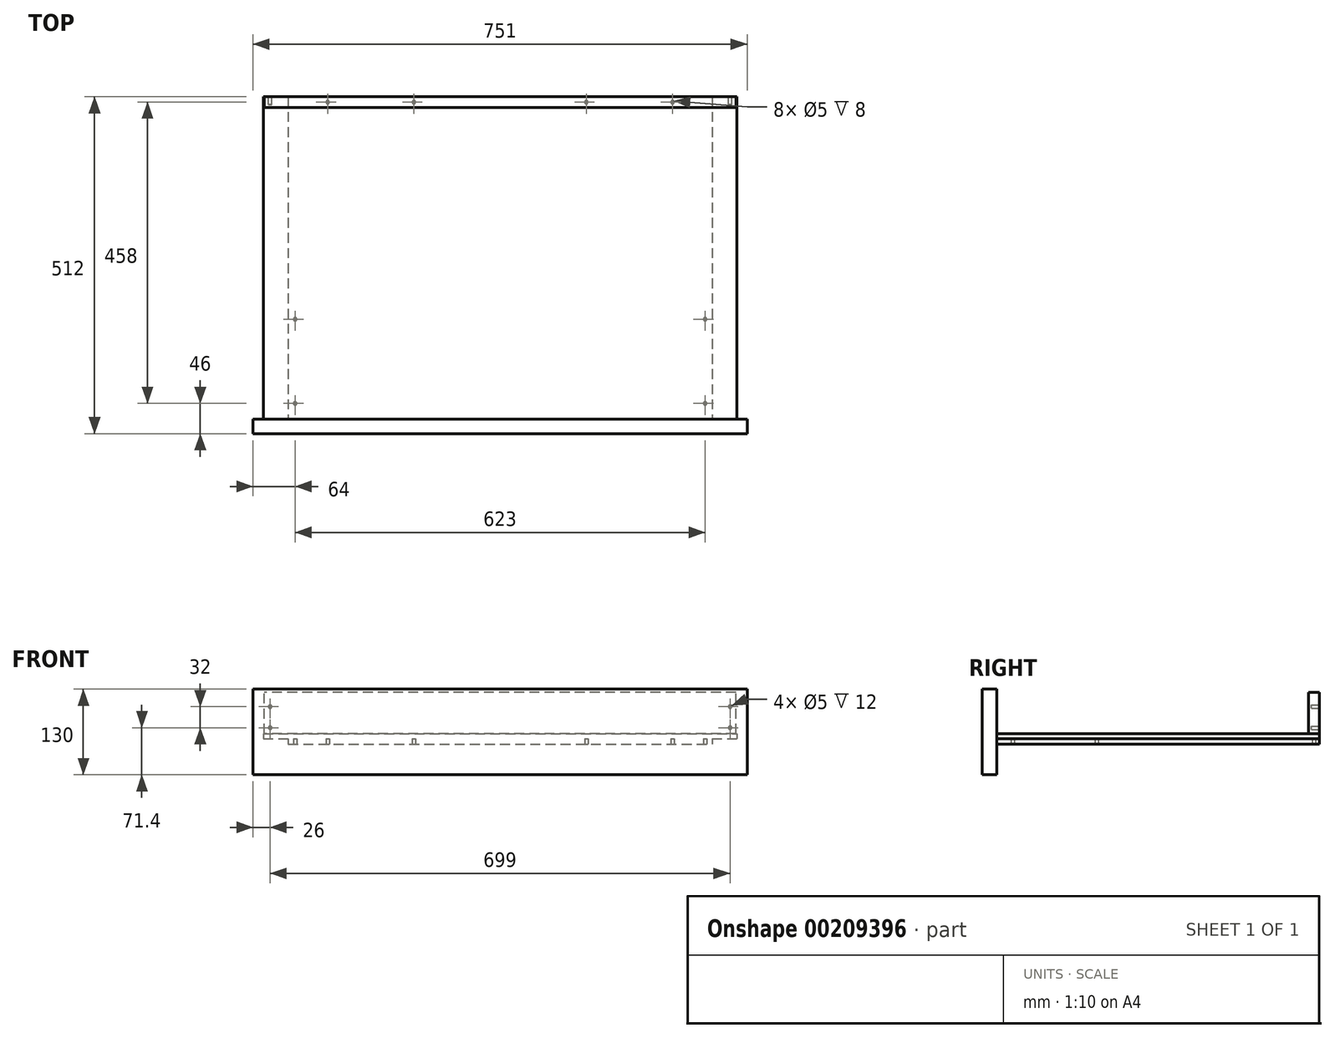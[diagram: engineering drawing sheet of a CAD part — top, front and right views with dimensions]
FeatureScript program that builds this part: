
annotation { "Feature Type Name" : "Feature", "Feature Type Description" : "" }
export const myFeature = defineFeature(function(context is Context, id is Id, definition is map)
    precondition{}
    {
        {
            assignVariable(context, id + "F0", {"name" : "P_DRAWER", "anyValue" : 490});
        }
        {
            var Q0;
            Q0=qCreatedBy(makeId("Front.planeOp"),FACE);
            var sketch = newSketch(context, id + "F1", { "sketchPlane" : qUnion([Q0])});
            skLineSegment(sketch, "E0.bottom", {"start": v(377.5, -360.5) * mm, "end": v(-377.5, -360.5) * mm});
            skLineSegment(sketch, "E0.top", {"start": v(377.5, 360.5) * mm, "end": v(-377.5, 360.5) * mm});
            skLineSegment(sketch, "E0.left", {"start": v(377.5, -360.5) * mm, "end": v(377.5, 360.5) * mm});
            skLineSegment(sketch, "E0.right", {"start": v(-377.5, -360.5) * mm, "end": v(-377.5, 360.5) * mm});
            skPoint(sketch, "E0.middle", {"position": v(0, 0) * mm});
            skSolve(sketch);
        }
        {
            var Q0;
            Q0=qCreatedBy(makeId("Front.planeOp"),FACE);
            var sketch = newSketch(context, id + "F2", { "sketchPlane" : qUnion([Q0])});
            skLineSegment(sketch, "E1.bottom", {"start": v(360, -336.1) * mm, "end": v(-360, -336.1) * mm});
            skLineSegment(sketch, "E1.top", {"start": v(360, -320.1) * mm, "end": v(-360, -320.1) * mm});
            skLineSegment(sketch, "E1.left", {"start": v(360, -336.1) * mm, "end": v(360, -320.1) * mm});
            skLineSegment(sketch, "E1.right", {"start": v(-360, -336.1) * mm, "end": v(-360, -320.1) * mm});
            skPoint(sketch, "E1.middle", {"position": v(0, -328.1) * mm});
            skLineSegment(sketch, "E2", {"start": v(-249.9, -252.5) * mm, "end": v(251.2, -252.5) * mm, "construction": true});
            skSolve(sketch);
        }
        {
            var Q0;
            Q0=makeQuery(id+"F1.imprint","IMPRINT",FACE,{"disambiguationData":[TD([[makeQuery(id+"F1.imprint","IMPRINT",EDGE,{"derivedFrom":sQuery(id+"F1.wireOp",EDGE,"E0.bottom")}),-1.0]])]});
            var sketch = newSketch(context, id + "F3", { "sketchPlane" : qUnion([Q0])});
            skLineSegment(sketch, "E3.bottom", {"start": v(-375.5, -252.5) * mm, "end": v(375.5, -252.5) * mm});
            skLineSegment(sketch, "E3.top", {"start": v(-375.5, -382.5) * mm, "end": v(375.5, -382.5) * mm});
            skLineSegment(sketch, "E3.left", {"start": v(-375.5, -252.5) * mm, "end": v(-375.5, -382.5) * mm});
            skLineSegment(sketch, "E3.right", {"start": v(375.5, -252.5) * mm, "end": v(375.5, -382.5) * mm});
            skLineSegment(sketch, "E4", {"start": v(0, 0) * mm, "end": v(0, -75.46) * mm, "construction": true});
            skCircle(sketch, "E5", {"center": v(-363.5, -277.5) * mm, "radius": 5 * mm, "construction": true});
            skCircle(sketch, "E6", {"center": v(-363.5, -309.5) * mm, "radius": 5 * mm, "construction": true});
            skCircle(sketch, "E7.MirrorC", {"center": v(363.5, -277.5) * mm, "radius": 5 * mm, "construction": true});
            skCircle(sketch, "E8.MirrorC", {"center": v(363.5, -309.5) * mm, "radius": 5 * mm, "construction": true});
            skSolve(sketch);
        }
        {
            var Q0;
            Q0=qCreatedBy(makeId("Front.planeOp"),FACE);
            cPlane(context, id + "F4", {"entities" : qUnion([Q0]), "cplaneType" : CPlaneType.OFFSET, "offset" : (getVariable(context, 'P_DRAWER')) * mm, "oppositeDirection" : true, "width" : 150 * mm, "height" : 150 * mm});
        }
        {
            var Q0;
            Q0=qCreatedBy(id+"F4.planeOp",FACE);
            var sketch = newSketch(context, id + "F5", { "sketchPlane" : qUnion([Q0])});
            skLineSegment(sketch, "E9.bottom", {"start": v(358.5, -320.1) * mm, "end": v(-358.5, -320.1) * mm});
            skLineSegment(sketch, "E9.top", {"start": v(358.5, -257.1) * mm, "end": v(-358.5, -257.1) * mm});
            skLineSegment(sketch, "E9.left", {"start": v(358.5, -320.1) * mm, "end": v(358.5, -257.1) * mm});
            skLineSegment(sketch, "E9.right", {"start": v(-358.5, -320.1) * mm, "end": v(-358.5, -257.1) * mm});
            skPoint(sketch, "E9.middle", {"position": v(0, -288.6) * mm});
            skCircle(sketch, "E10", {"center": v(-349.5, -311.1) * mm, "radius": 2.5 * mm, "construction": true});
            skCircle(sketch, "E11", {"center": v(-349.5, -279.1) * mm, "radius": 2.5 * mm, "construction": true});
            skCircle(sketch, "E12", {"center": v(-349.5, -247.1) * mm, "radius": 2.5 * mm, "construction": true});
            skCircle(sketch, "E13.MirrorC", {"center": v(349.5, -247.1) * mm, "radius": 2.5 * mm, "construction": true});
            skCircle(sketch, "E14.MirrorC", {"center": v(349.5, -279.1) * mm, "radius": 2.5 * mm, "construction": true});
            skCircle(sketch, "E15.MirrorC", {"center": v(349.5, -311.1) * mm, "radius": 2.5 * mm, "construction": true});
            skSolve(sketch);
        }
        {
            var Q0;
            Q0=qCreatedBy(makeId("Front.planeOp"),FACE);
            var sketch = newSketch(context, id + "F6", { "sketchPlane" : qUnion([Q0])});
            skLineSegment(sketch, "E16.0", {"start": v(360, -336.1) * mm, "end": v(-360, -336.1) * mm});
            skLineSegment(sketch, "E16.1", {"start": v(360, -320.1) * mm, "end": v(-360, -320.1) * mm});
            skLineSegment(sketch, "E16.2", {"start": v(360, -336.1) * mm, "end": v(360, -320.1) * mm});
            skLineSegment(sketch, "E16.3", {"start": v(-360, -336.1) * mm, "end": v(-360, -320.1) * mm});
            skPoint(sketch, "E16.4", {"position": v(0, -328.1) * mm});
            skLineSegment(sketch, "E16.5", {"start": v(-249.9, -252.5) * mm, "end": v(251.2, -252.5) * mm, "construction": true});
            skSolve(sketch);
        }
        {
            var Q0;
            Q0=qSketchRegion(id+"F6",true);
            var Q1;
            Q1=qCreatedBy(id+"F4.planeOp",FACE);
            extrude(context, id + "F7", {"entities" : qUnion([Q0]), "endBound" : BoundingType.UP_TO_SURFACE, "oppositeDirection" : true, "endBoundEntityFace" : qUnion([Q1]), "depth" : (getVariable(context, 'P_DRAWER')) * mm});
        }
        {
            var Q0;
            Q0=makeQuery(id+"F7.opExtrude","SWEPT_FACE",FACE,{"disambiguationData":[OSD([sQuery(id+"F6.wireOp",EDGE,"E16.0")])]});
            var sketch = newSketch(context, id + "F8", { "sketchPlane" : qUnion([Q0])});
            skLineSegment(sketch, "E17.bottom", {"start": v(-360, -490) * mm, "end": v(-322, -490) * mm});
            skLineSegment(sketch, "E17.top", {"start": v(-360, 0) * mm, "end": v(-322, 0) * mm});
            skLineSegment(sketch, "E17.left", {"start": v(-360, -490) * mm, "end": v(-360, 0) * mm});
            skLineSegment(sketch, "E17.right", {"start": v(-322, -490) * mm, "end": v(-322, 0) * mm});
            skLineSegment(sketch, "E18.bottom", {"start": v(360, -490) * mm, "end": v(322, -490) * mm});
            skLineSegment(sketch, "E18.top", {"start": v(360, 0) * mm, "end": v(322, 0) * mm});
            skLineSegment(sketch, "E18.left", {"start": v(360, -490) * mm, "end": v(360, 0) * mm});
            skLineSegment(sketch, "E18.right", {"start": v(322, -490) * mm, "end": v(322, 0) * mm});
            skCircle(sketch, "E19", {"center": v(-311.5, -24) * mm, "radius": 2.5 * mm});
            skCircle(sketch, "E20", {"center": v(-311.5, -152) * mm, "radius": 2.5 * mm});
            skLineSegment(sketch, "E21", {"start": v(0, 0) * mm, "end": v(0, -490) * mm, "construction": true});
            skCircle(sketch, "E22.MirrorC", {"center": v(311.5, -152) * mm, "radius": 2.5 * mm});
            skCircle(sketch, "E23.MirrorC", {"center": v(311.5, -24) * mm, "radius": 2.5 * mm});
            skCircle(sketch, "E24", {"center": v(-262, -482) * mm, "radius": 2.5 * mm});
            skCircle(sketch, "E25", {"center": v(-131, -482) * mm, "radius": 2.5 * mm});
            skLineSegment(sketch, "E26", {"start": v(-262, -482) * mm, "end": v(-131, -482) * mm, "construction": true});
            skLineSegment(sketch, "E27", {"start": v(-262, -482) * mm, "end": v(-322, -482) * mm, "construction": true});
            skLineSegment(sketch, "E28", {"start": v(-131, -482) * mm, "end": v(0, -482) * mm, "construction": true});
            skCircle(sketch, "E29.MirrorC", {"center": v(131, -482) * mm, "radius": 2.5 * mm});
            skCircle(sketch, "E30.MirrorC", {"center": v(262, -482) * mm, "radius": 2.5 * mm});
            skSolve(sketch);
        }
        {
            var Q0;
            Q0=qSketchRegion(id+"F8",true);
            extrude(context, id + "F9", {"entities" : qUnion([Q0]), "operationType" : NewBodyOperationType.REMOVE, "oppositeDirection" : true, "depth" : 8 * mm});
        }
        {
            var Q0;
            Q0=qSketchRegion(id+"F5",true);
            extrude(context, id + "F10", {"entities" : qUnion([Q0]), "depth" : 16 * mm});
        }
        {
            var Q0;
            Q0=makeQuery(id+"F5.imprint","IMPRINT",FACE,{"disambiguationData":[TD([[makeQuery(id+"F5.imprint","IMPRINT",EDGE,{"derivedFrom":sQuery(id+"F5.wireOp",EDGE,"E9.bottom")}),-1.0]])]});
            var sketch = newSketch(context, id + "F11", { "sketchPlane" : qUnion([Q0])});
            skCircle(sketch, "E31.0", {"center": v(349.5, -311.1) * mm, "radius": 2.5 * mm});
            skCircle(sketch, "E31.1", {"center": v(349.5, -279.1) * mm, "radius": 2.5 * mm});
            skCircle(sketch, "E31.2", {"center": v(349.5, -247.1) * mm, "radius": 2.5 * mm});
            skCircle(sketch, "E31.3", {"center": v(-349.5, -247.1) * mm, "radius": 2.5 * mm});
            skCircle(sketch, "E31.4", {"center": v(-349.5, -279.1) * mm, "radius": 2.5 * mm});
            skCircle(sketch, "E31.5", {"center": v(-349.5, -311.1) * mm, "radius": 2.5 * mm});
            skSolve(sketch);
        }
        {
            var Q0;
            Q0=qSketchRegion(id+"F11",true);
            extrude(context, id + "F12", {"entities" : qUnion([Q0]), "operationType" : NewBodyOperationType.REMOVE, "depth" : 12 * mm});
        }
        {
            var Q0;
            Q0=qSketchRegion(id+"F3",true);
            extrude(context, id + "F13", {"entities" : qUnion([Q0]), "depth" : 22 * mm});
        }
    });
